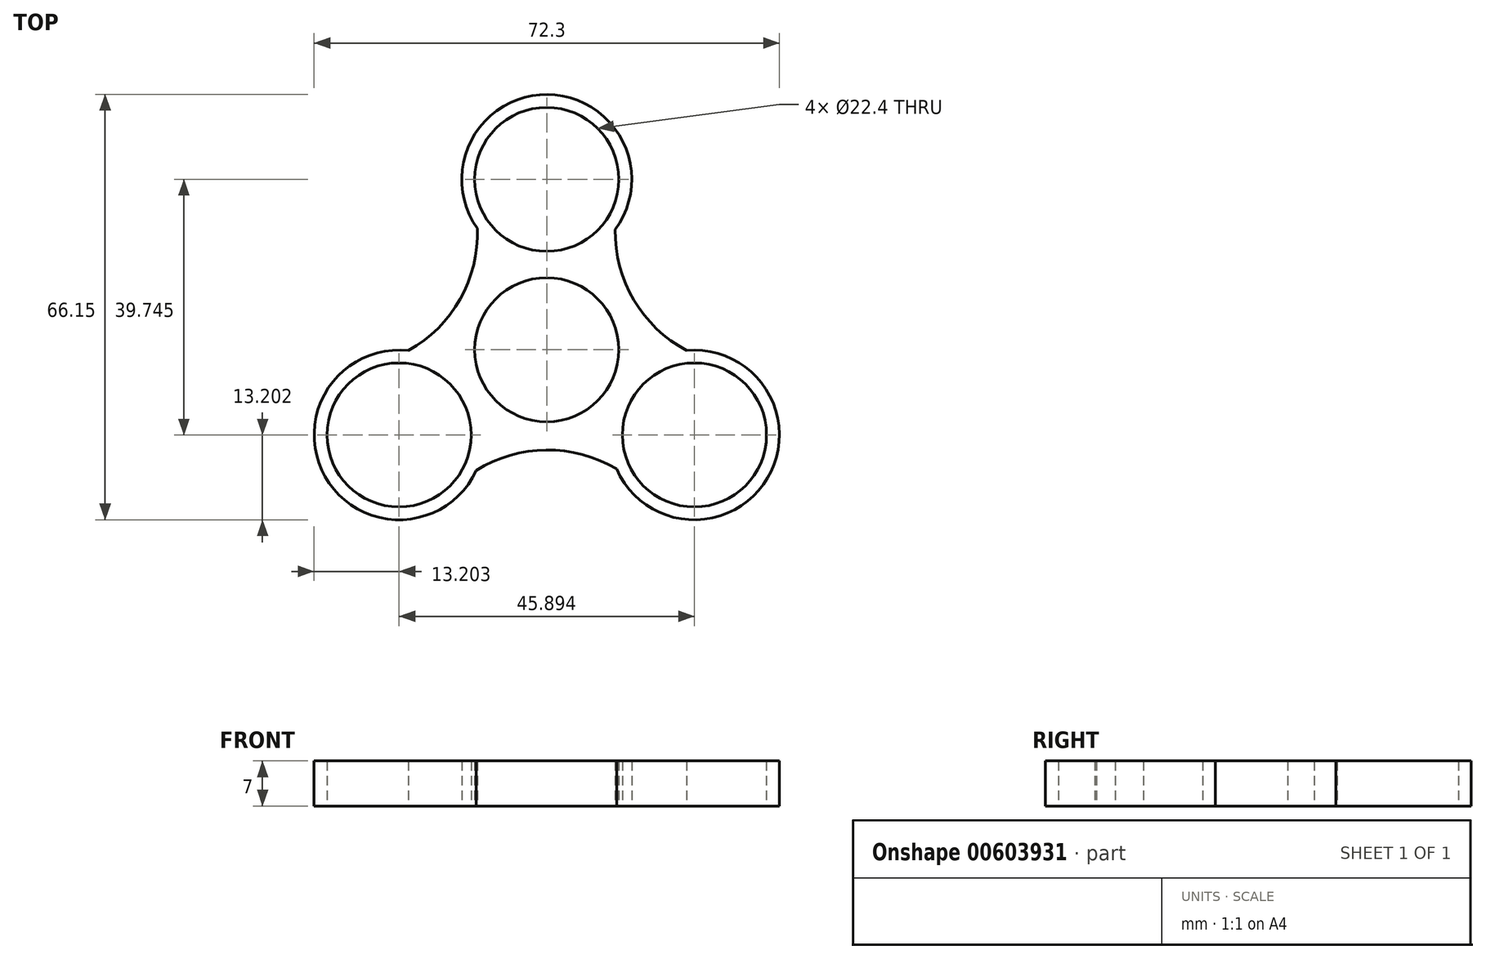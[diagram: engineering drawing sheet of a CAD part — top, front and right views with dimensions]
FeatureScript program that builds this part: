
annotation { "Feature Type Name" : "Feature", "Feature Type Description" : "" }
export const myFeature = defineFeature(function(context is Context, id is Id, definition is map)
    precondition{}
    {
        {
            var Q0;
            Q0=qCreatedBy(makeId("Top.planeOp"),FACE);
            var sketch = newSketch(context, id + "F0", { "sketchPlane" : qUnion([Q0])});
            skCircle(sketch, "E0", {"center": v(0, 0) * mm, "radius": 11.2 * mm});
            skCircle(sketch, "E1", {"center": v(0, 26.5) * mm, "radius": 11.2 * mm});
            skArc(sketch, "E2", {"start": v(10.63, 18.68) * mm, "mid": v(0.12, 39.7) * mm, "end": v(-10.77, 18.87) * mm});
            skArc(sketch, "E3.1.0", {"start": v(-21.5, -0.13) * mm, "mid": v(-34.44, -19.75) * mm, "end": v(-10.95, -18.76) * mm});
            skCircle(sketch, "E3.1.1", {"center": v(-22.95, -13.25) * mm, "radius": 11.2 * mm});
            skArc(sketch, "E3.2.0", {"start": v(10.86, -18.55) * mm, "mid": v(34.32, -19.95) * mm, "end": v(21.73, -0.1) * mm});
            skCircle(sketch, "E3.2.1", {"center": v(22.95, -13.25) * mm, "radius": 11.2 * mm});
            skArc(sketch, "E4", {"start": v(-21.5, -0.13) * mm, "mid": v(-13.46, 7.86) * mm, "end": v(-10.77, 18.87) * mm});
            skArc(sketch, "E5.1.0", {"start": v(10.86, -18.55) * mm, "mid": v(-0.08, -15.59) * mm, "end": v(-10.95, -18.76) * mm});
            skArc(sketch, "E5.2.0", {"start": v(10.63, 18.68) * mm, "mid": v(13.54, 7.73) * mm, "end": v(21.73, -0.1) * mm});
            skSolve(sketch);
        }
        {
            var Q0;
            Q0=makeQuery(id+"F0.imprint","IMPRINT",FACE,{"disambiguationData":[TD([[makeQuery(id+"F0.imprint","IMPRINT",EDGE,{"derivedFrom":sQuery(id+"F0.wireOp",EDGE,"E0")}),-1.0]])]});
            extrude(context, id + "F1", {"entities" : qUnion([Q0]), "depth" : 7 * mm, "offsetDistance" : 25 * mm});
        }
    });
